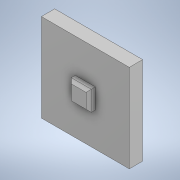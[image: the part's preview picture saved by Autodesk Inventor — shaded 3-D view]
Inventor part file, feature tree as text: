
AUTODESK INVENTOR PART (.ipt)
format: ipt  version: 2022 (Build 260153000, 153)  size: 185,856 bytes
history: native  units: in
note: dims shown in document units (in); Inventor stores cm internally (conversion verified against a paired STEP export)
features: extrude x2, sketch x2, chamfer x1
ambient origin geometry x8: Origin, YZ Plane, XZ Plane, XY Plane, X Axis, Y Axis, Z Axis, Center Point
bodies: Solid1 (feature_tree), Body2 (feature_tree)
feature tree (5):
  extrude  "Extrusion1"  Depth=0.0295in
  extrude  "Extrusion2"  Depth=0.0098in TaperAngle=0.0deg
  chamfer  "Chamfer1"  Distance=0.0039in Angle=45.0deg
  sketch  "Sketch1"  dims[d0=0.2313in d1=0.0in d2=0.0295in]
  sketch  "Sketch3"  dims[d3=0.0295in d4=0.0098in d5=0.0in d6=0.0039in d7=0.0787in d8=45.0deg]
